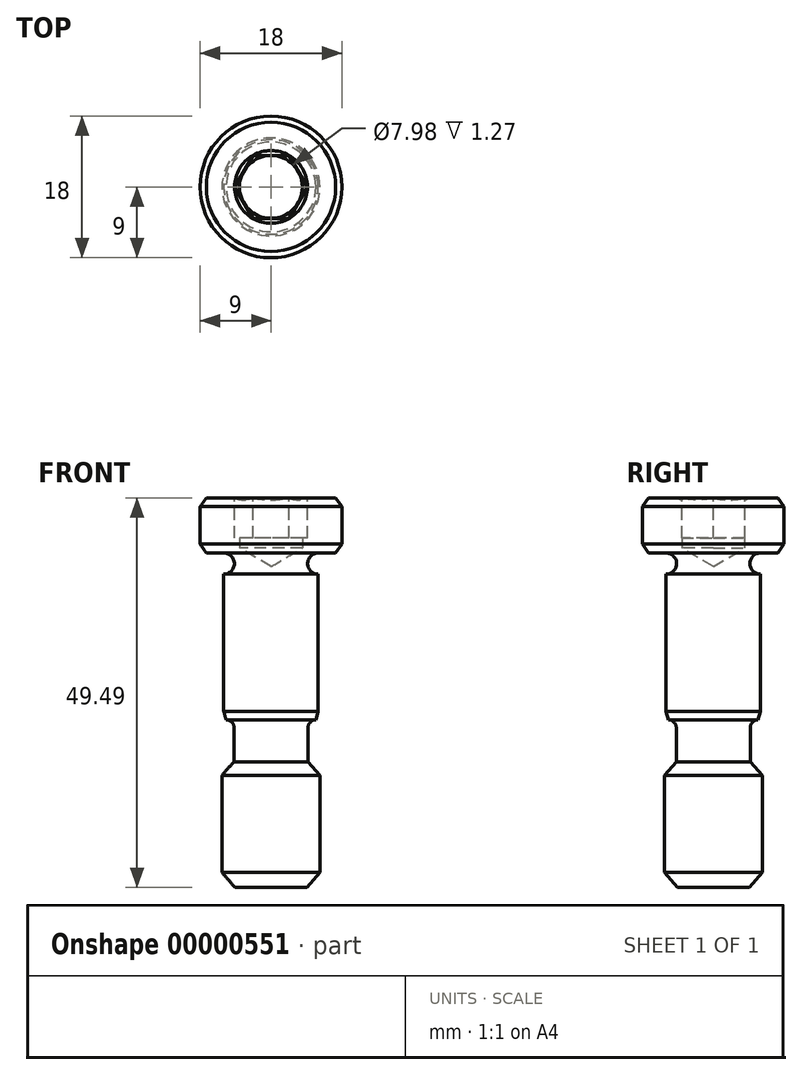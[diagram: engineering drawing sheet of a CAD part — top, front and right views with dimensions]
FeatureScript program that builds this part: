
annotation { "Feature Type Name" : "Feature", "Feature Type Description" : "" }
export const myFeature = defineFeature(function(context is Context, id is Id, definition is map)
    precondition{}
    {
        {
            var Q0;
            Q0 = qCreatedBy(makeId("Front.planeOp"), FACE);
            var sketch = newSketch(context, id + "F0", { "sketchPlane" : qUnion([Q0])});
            skLineSegment(sketch, "E0", {"start": v(0, 0) * mm, "end": v(8.21, 0) * mm});
            skLineSegment(sketch, "E1", {"start": v(9, -1.12) * mm, "end": v(9, -5.89) * mm});
            skLineSegment(sketch, "E2", {"start": v(9, -5.89) * mm, "end": v(8.21, -7) * mm});
            skLineSegment(sketch, "E3", {"start": v(8.21, -7) * mm, "end": v(6, -7) * mm});
            skArc(sketch, "E4", {"start": v(6, -7) * mm, "mid": v(4.66, -8.35) * mm, "end": v(6, -9.7) * mm});
            skLineSegment(sketch, "E5", {"start": v(6, -9.7) * mm, "end": v(6, -27.1) * mm});
            skLineSegment(sketch, "E6", {"start": v(6, -27.1) * mm, "end": v(5.7, -28.2) * mm});
            skLineSegment(sketch, "E7", {"start": v(4.7, -29.2) * mm, "end": v(4.7, -33.52) * mm});
            skLineSegment(sketch, "E8", {"start": v(4.7, -33.52) * mm, "end": v(6.23, -35.24) * mm});
            skLineSegment(sketch, "E9", {"start": v(6.23, -35.24) * mm, "end": v(6.23, -47.59) * mm});
            skLineSegment(sketch, "E10", {"start": v(6.23, -47.59) * mm, "end": v(4.57, -49.5) * mm});
            skLineSegment(sketch, "E11", {"start": v(4.57, -49.5) * mm, "end": v(0, -49.5) * mm});
            skLineSegment(sketch, "E12", {"start": v(0, -49.5) * mm, "end": v(0, 0) * mm});
            skLineSegment(sketch, "E13", {"start": v(8.21, 0) * mm, "end": v(9, -1.12) * mm});
            skArc(sketch, "E14", {"start": v(5.7, -28.2) * mm, "mid": v(5, -28.5) * mm, "end": v(4.7, -29.2) * mm});
            skLineSegment(sketch, "E15", {"start": v(3.99, -6.35) * mm, "end": v(0, -8.75) * mm});
            skLineSegment(sketch, "E16", {"start": v(3.99, -6.35) * mm, "end": v(3.99, 0) * mm});
            skSolve(sketch);
        }
        {
            var Q0;
            Q0=makeQuery(id+"F0.imprint","IMPRINT",FACE,{"disambiguationData":[TD([[makeQuery(id+"F0.imprint","IMPRINT",EDGE,{"derivedFrom":sQuery(id+"F0.wireOp",EDGE,"E1")}),-1.0]])]});
            var Q1;
            Q1=sQuery(id+"F0.wireOp",EDGE,"E12");
            revolve(context, id + "F1", {"entities" : qUnion([Q0]), "axis" : qUnion([Q1]), "revolveType" : RevolveType.FULL});
        }
        {
            var Q0;
            Q0 = qCreatedBy(makeId("Top.planeOp"), FACE);
            var sketch = newSketch(context, id + "F2", { "sketchPlane" : qUnion([Q0])});
            skCircle(sketch, "E17", {"center": v(0, 0) * mm, "radius": 4.62 * mm, "construction": true});
            skLineSegment(sketch, "E18", {"start": v(-2.3, -4) * mm, "end": v(-4.62, 0) * mm});
            skLineSegment(sketch, "E19", {"start": v(-4.62, 0) * mm, "end": v(-2.3, 4) * mm});
            skLineSegment(sketch, "E20", {"start": v(-2.3, 4) * mm, "end": v(2.3, 4) * mm});
            skLineSegment(sketch, "E21", {"start": v(2.3, 4) * mm, "end": v(4.62, 0) * mm});
            skLineSegment(sketch, "E22", {"start": v(4.62, 0) * mm, "end": v(2.3, -4) * mm});
            skLineSegment(sketch, "E23", {"start": v(2.3, -4) * mm, "end": v(-2.3, -4) * mm});
            skSolve(sketch);
        }
        {
            var Q0;
            Q0=makeQuery(id+"F2.imprint","IMPRINT",FACE,{"disambiguationData":[TD([[makeQuery(id+"F2.imprint","IMPRINT",EDGE,{"derivedFrom":sQuery(id+"F2.wireOp",EDGE,"E18")}),-1.0]])]});
            extrude(context, id + "F3", {"entities" : qUnion([Q0]), "operationType" : NewBodyOperationType.REMOVE, "oppositeDirection" : true, "depth" : 5.08 * mm});
        }
        {
            var Q0;
            Q0 = qCreatedBy(makeId("Front.planeOp"), FACE);
            var sketch = newSketch(context, id + "F4", { "sketchPlane" : qUnion([Q0])});
            skPoint(sketch, "E24.0", {"position": v(4.62, 0) * mm});
            skPoint(sketch, "E25.1", {"position": v(-4.62, 0) * mm});
            skArc(sketch, "E26", {"start": v(-4.62, 0) * mm, "mid": v(0, -1) * mm, "end": v(4.62, 0) * mm});
            skLineSegment(sketch, "E27", {"start": v(0, 0) * mm, "end": v(0, -1) * mm});
            skLineSegment(sketch, "E28", {"start": v(-4.62, 0) * mm, "end": v(0, 0) * mm});
            skSolve(sketch);
        }
        {
            var Q0;
            {var subQ1=sQuery(id+"F4.wireOp",EDGE,"E27");Q0=makeQuery(id+"F4.imprint","IMPRINT",FACE,{"disambiguationData":[TD([[makeQuery(id+"F4.imprint","IMPRINT",EDGE,{"derivedFrom":subQ1}),-1.0]])]});}
            var Q1;
            Q1=sQuery(id+"F4.wireOp",EDGE,"E27");
            revolve(context, id + "F5", {"operationType" : NewBodyOperationType.REMOVE, "entities" : qUnion([Q0]), "axis" : qUnion([Q1]), "revolveType" : RevolveType.FULL, "oppositeDirection" : true});
        }
    });
